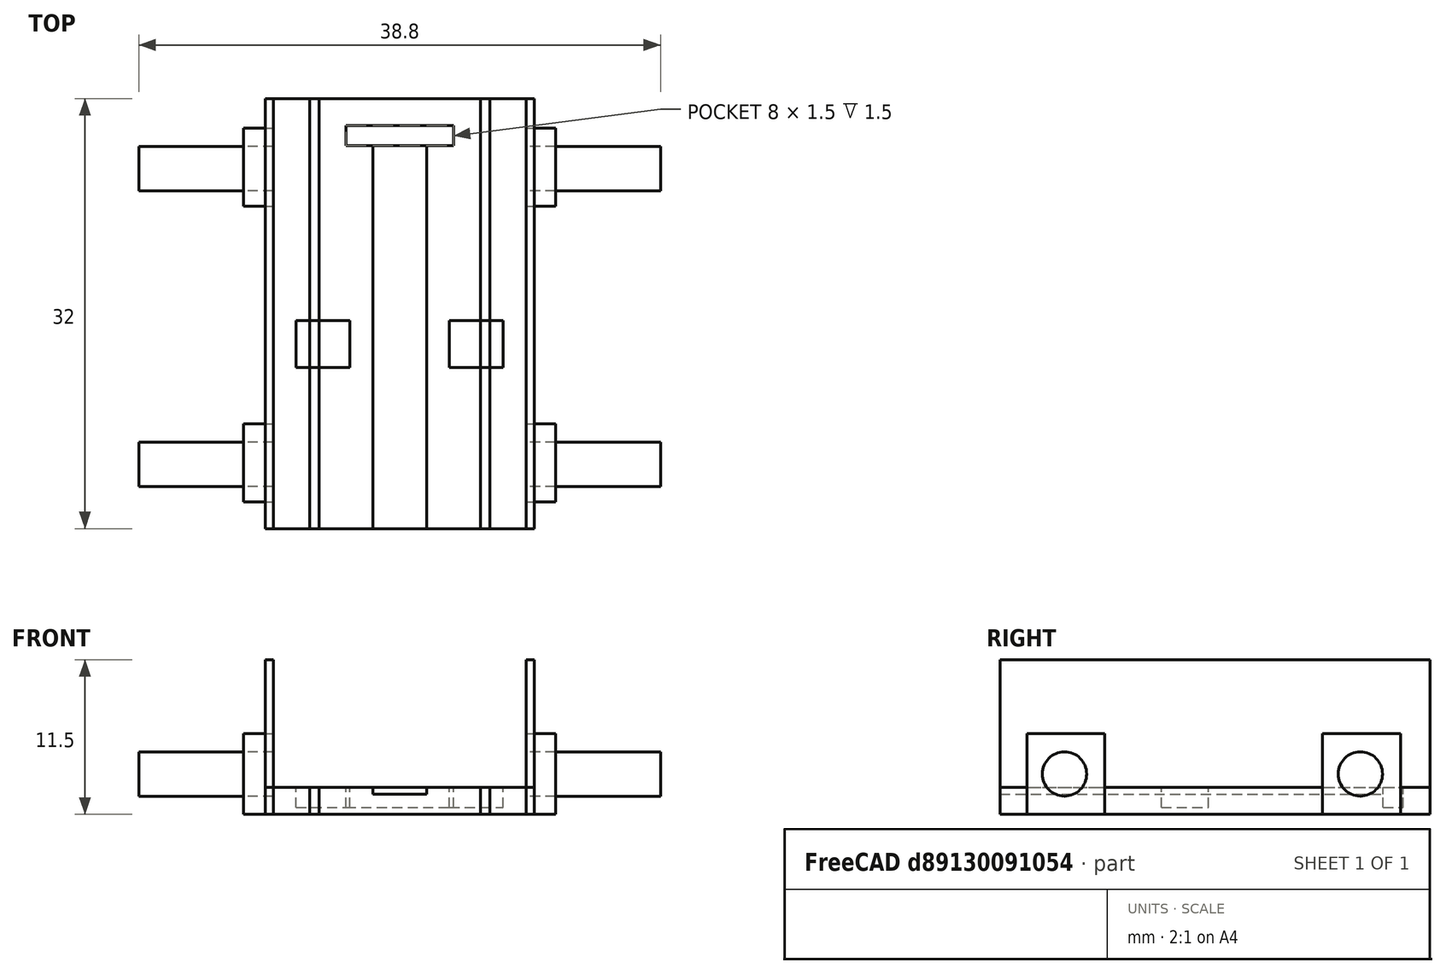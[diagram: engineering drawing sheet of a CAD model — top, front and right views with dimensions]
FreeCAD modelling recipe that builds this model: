
FCSTD DOCUMENT  (FreeCAD 0.18R14555 (Git shallow))
Label: power-connector-mounter
License: All rights reserved
LicenseURL: http://en.wikipedia.org/wiki/All_rights_reserved
objects: Part::Box×13, Part::Cylinder×4, Part::Cut×2, Part::MultiFuse×1
note: 20 computed .brp shape members not serialized (recipe doc carries the construction recipe); baked Part::Feature solids carry a one-line shape summary decoded from their .brp

FEATURE [Part::Box] Box  label="Cube"
  AttacherType = Attacher::AttachEngine3D
  Height = 2
  Length = 13.4
  Placement = pos=(-6.7,0,0) rot=(0,0,1;0rad)
  Width = 32
FEATURE [Part::Box] Box001  label="Cube001"
  AttacherType = Attacher::AttachEngine3D
  Height = 0.5
  Length = 4
  Placement = pos=(-2,0,1.5) rot=(0,0,1;0rad)
  Width = 30
FEATURE [Part::Cut] Cut
  Base = -> Box
  Tool = -> Box001
FEATURE [Part::Box] Box002  label="stopper-2"
  AttacherType = Attacher::AttachEngine3D
  Height = 1.5
  Length = 4
  Placement = pos=(-7.7,12,0.5) rot=(0,0,1;0rad)
  Width = 3.5
FEATURE [Part::Box] Box003  label="stopper-1"
  AttacherType = Attacher::AttachEngine3D
  Height = 1.5
  Length = 4
  Placement = pos=(3.7,12,0.5) rot=(0,0,1;0rad)
  Width = 3.5
FEATURE [Part::Box] Box004  label="Cube004"
  AttacherType = Attacher::AttachEngine3D
  Height = 1.5
  Length = 8
  Placement = pos=(-4,28.5,0.5) rot=(0,0,1;0rad)
  Width = 1.5
FEATURE [Part::Cut] Cut001
  Base = -> Cut
  Tool = -> Box004
FEATURE [Part::Box] Box005  label="Cube005"
  AttacherType = Attacher::AttachEngine3D
  Height = 2
  Length = 4
  Placement = pos=(-10,0,0) rot=(0,0,1;0rad)
  Width = 32
FEATURE [Part::Box] Box006  label="Cube006"
  AttacherType = Attacher::AttachEngine3D
  Height = 2
  Length = 4
  Placement = pos=(6,0,0) rot=(0,0,1;0rad)
  Width = 32
FEATURE [Part::MultiFuse] Fusion001  label="stopper-cut"
  Shapes = -> [Box002,Box003]
FEATURE [Part::Box] Box007  label="Cube007"
  AttacherType = Attacher::AttachEngine3D
  Height = 11.5
  Length = 0.6
  Placement = pos=(-10,0,0) rot=(0,0,1;0rad)
  Width = 32
FEATURE [Part::Box] Box008  label="Cube008"
  AttacherType = Attacher::AttachEngine3D
  Height = 11.5
  Length = 0.6
  Placement = pos=(9.4,0,0) rot=(0,0,1;0rad)
  Width = 32
FEATURE [Part::Box] Box009  label="Cube009"
  AttacherType = Attacher::AttachEngine3D
  Height = 6
  Length = 2.2
  Placement = pos=(-11.6,2,0) rot=(0,0,1;0rad)
  Width = 5.8
FEATURE [Part::Box] Box010  label="Cube010"
  AttacherType = Attacher::AttachEngine3D
  Height = 6
  Length = 2.2
  Placement = pos=(9.4,2,0) rot=(0,0,1;0rad)
  Width = 5.8
FEATURE [Part::Box] Box011  label="Cube011"
  AttacherType = Attacher::AttachEngine3D
  Height = 6
  Length = 2.2
  Placement = pos=(-11.6,24,0) rot=(0,0,1;0rad)
  Width = 5.8
FEATURE [Part::Box] Box012  label="Cube012"
  AttacherType = Attacher::AttachEngine3D
  Height = 6
  Length = 2.2
  Placement = pos=(9.4,24,0) rot=(0,0,1;0rad)
  Width = 5.8
FEATURE [Part::Cylinder] Cylinder
  Angle = 360
  AttacherType = Attacher::AttachEngine3D
  Height = 10
  Placement = pos=(-9.4,4.8,3) rot=(0,-1,0;1.5708rad)
  Radius = 1.65
FEATURE [Part::Cylinder] Cylinder001
  Angle = 360
  AttacherType = Attacher::AttachEngine3D
  Height = 10
  Placement = pos=(19.4,26.8,3) rot=(0,-1,0;1.5708rad)
  Radius = 1.65
FEATURE [Part::Cylinder] Cylinder002
  Angle = 360
  AttacherType = Attacher::AttachEngine3D
  Height = 10
  Placement = pos=(-9.4,26.8,3) rot=(0,-1,0;1.5708rad)
  Radius = 1.65
FEATURE [Part::Cylinder] Cylinder003
  Angle = 360
  AttacherType = Attacher::AttachEngine3D
  Height = 10
  Placement = pos=(19.4,4.8,3) rot=(0,-1,0;1.5708rad)
  Radius = 1.65
